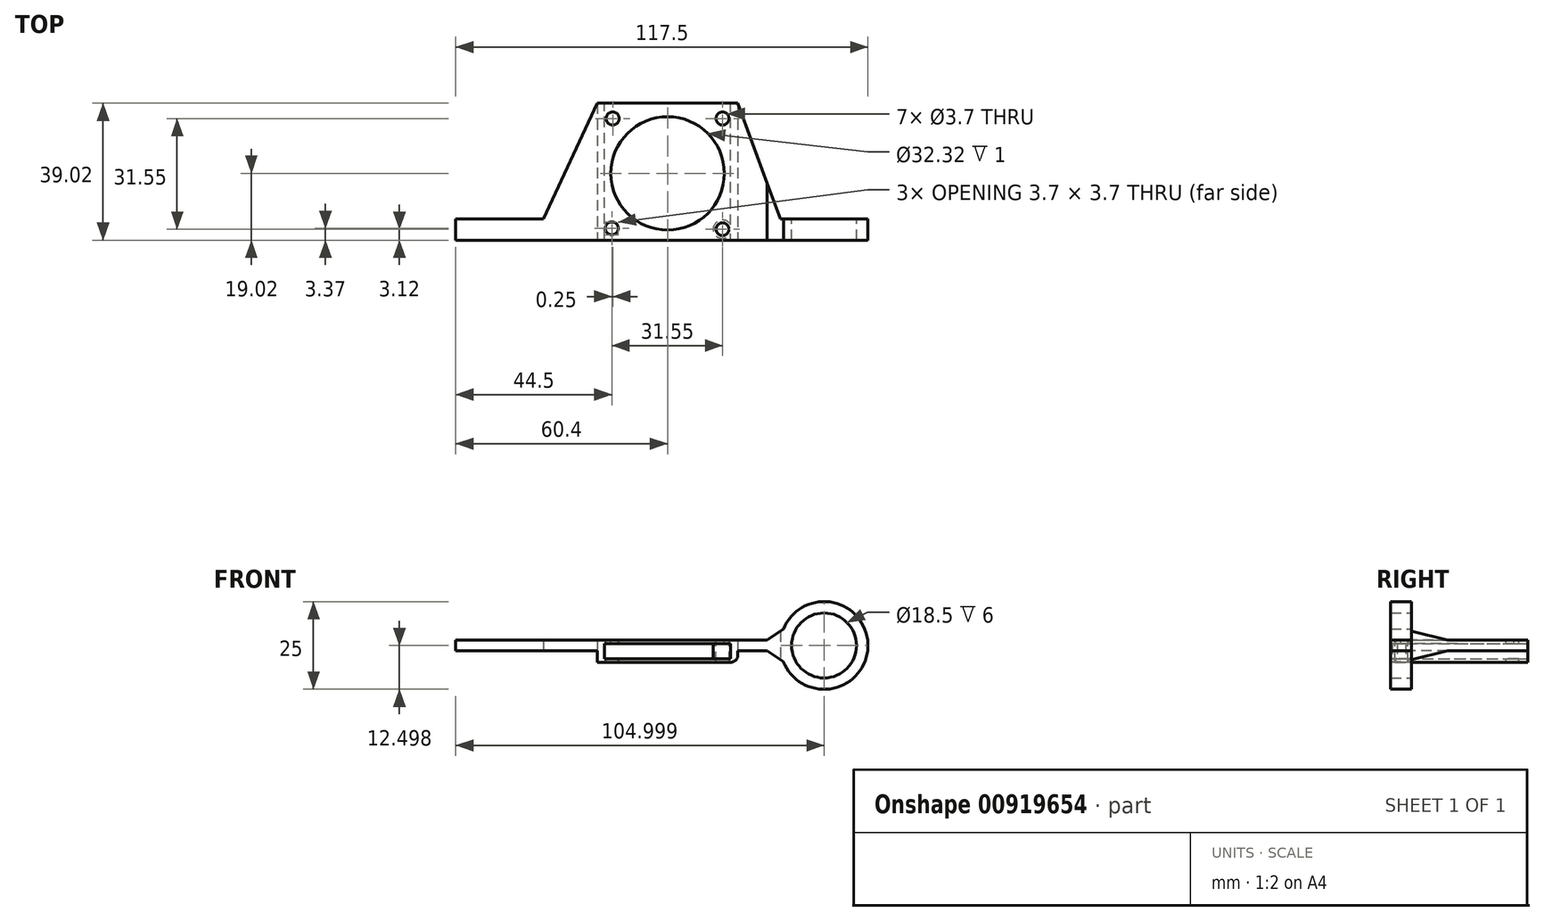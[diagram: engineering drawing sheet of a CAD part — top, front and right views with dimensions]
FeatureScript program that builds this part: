
annotation { "Feature Type Name" : "Feature", "Feature Type Description" : "" }
export const myFeature = defineFeature(function(context is Context, id is Id, definition is map)
    precondition{}
    {
        {
            var Q0;
            Q0=qCreatedBy(makeId("Top.planeOp"),FACE);
            var sketch = newSketch(context, id + "F0", { "sketchPlane" : qUnion([Q0])});
            skLineSegment(sketch, "E0", {"start": v(20, 20) * mm, "end": v(-20, 20) * mm});
            skLineSegment(sketch, "E1", {"start": v(48.76, 105.8) * mm, "end": v(3.76, 105.8) * mm});
            skLineSegment(sketch, "E2", {"start": v(20, 20) * mm, "end": v(32.1, -13.02) * mm});
            skLineSegment(sketch, "E3", {"start": v(57.1, -19.02) * mm, "end": v(57.1, -13.02) * mm});
            skLineSegment(sketch, "E4", {"start": v(57.1, -13.02) * mm, "end": v(32.1, -13.02) * mm});
            skLineSegment(sketch, "E5", {"start": v(-20, 20) * mm, "end": v(-35.4, -13.02) * mm});
            skLineSegment(sketch, "E6", {"start": v(-35.4, -13.02) * mm, "end": v(-60.4, -13.02) * mm});
            skLineSegment(sketch, "E7", {"start": v(-60.4, -13.02) * mm, "end": v(-60.4, -19.02) * mm});
            skLineSegment(sketch, "E8", {"start": v(-60.4, -19.02) * mm, "end": v(57.1, -19.02) * mm});
            skSolve(sketch);
        }
        {
            var Q0;
            Q0 = qSketchRegion(id + "F0", true);
            extrude(context, id + "F1", {"entities" : qUnion([Q0]), "depth" : 3 * mm, "offsetDistance" : 25 * mm});
        }
        {
            var Q0;
            Q0=makeQuery(id+"F1.opExtrude","SWEPT_FACE",FACE,{"disambiguationData":[OSD([sQuery(id+"F0.wireOp",EDGE,"E4")])]});
            var sketch = newSketch(context, id + "F2", { "sketchPlane" : qUnion([Q0])});
            skCircle(sketch, "E9", {"center": v(-44.6, 1.46) * mm, "radius": 12.5 * mm});
            skSolve(sketch);
        }
        {
            var Q0;
            Q0 = qSketchRegion(id + "F2", true);
            extrude(context, id + "F3", {"entities" : qUnion([Q0]), "operationType" : NewBodyOperationType.ADD, "oppositeDirection" : true, "depth" : 6 * mm, "offsetDistance" : 25 * mm});
        }
        {
            var Q0;
            Q0=makeQuery(id+"Fj0goD7DDU6lidK_1.boolean.opBoolean","MERGE",FACE,{"derivedFrom":[makeQuery(id+"F1.opExtrude","SWEPT_FACE",FACE,{"disambiguationData":[OSD([sQuery(id+"F0.wireOp",EDGE,"E4")])]}),makeQuery(id+"Fj0goD7DDU6lidK_1.opExtrude","CAP_FACE",FACE,{"disambiguationData":[OSD([sQuery(id+"F2.wireOp",EDGE,"E9")])],"isStart":true})]});
            var sketch = newSketch(context, id + "F4", { "sketchPlane" : qUnion([Q0])});
            skCircle(sketch, "E10", {"center": v(-44.6, 1.46) * mm, "radius": 9.25 * mm});
            skSolve(sketch);
        }
        {
            var Q0;
            Q0 = qSketchRegion(id + "F4", true);
            extrude(context, id + "F5", {"entities" : qUnion([Q0]), "operationType" : NewBodyOperationType.REMOVE, "oppositeDirection" : true, "depth" : 25 * mm, "offsetDistance" : 25 * mm});
        }
        {
            var Q0;
            {var subQ0=sQuery(id+"F0.wireOp",EDGE,"E8");var subQ1=sQuery(id+"F0.wireOp",EDGE,"E7");var subQ2=sQuery(id+"F0.wireOp",EDGE,"E6");var subQ3=sQuery(id+"F0.wireOp",EDGE,"E0");var subQ5=sQuery(id+"F0.wireOp",EDGE,"E4");var subQ6=sQuery(id+"F0.wireOp",EDGE,"E2");var subQ7=sQuery(id+"F0.wireOp",EDGE,"E5");Q0=makeQuery(id+"F3.boolean.opBoolean","SPLIT",FACE,{"disambiguationData":[TD([makeQuery(id+"F1.opExtrude","SWEPT_FACE",FACE,{"disambiguationData":[OSD([subQ3])]})])],"derivedFrom":makeQuery(id+"F1.opExtrude","CAP_FACE",FACE,{"disambiguationData":[OSD([subQ3,subQ6,sQuery(id+"F0.wireOp",EDGE,"E3"),subQ5,subQ7,subQ2,subQ1,subQ0])],"isStart":false})});}
            var sketch = newSketch(context, id + "F6", { "sketchPlane" : qUnion([Q0])});
            skCircle(sketch, "E11", {"center": v(0, 0) * mm, "radius": 16.16 * mm});
            skSolve(sketch);
        }
        {
            var Q0;
            Q0=makeQuery(id+"F6.imprint","IMPRINT",FACE,{"disambiguationData":[TD([[makeQuery(id+"F6.imprint","IMPRINT",EDGE,{"derivedFrom":sQuery(id+"F6.wireOp",EDGE,"E11")}),1.0]])]});
            extrude(context, id + "F7", {"entities" : qUnion([Q0]), "operationType" : NewBodyOperationType.REMOVE, "oppositeDirection" : true, "depth" : 25 * mm, "offsetDistance" : 25 * mm});
        }
        {
            var Q0;
            Q0=qCreatedBy(makeId("Right.planeOp"),FACE);
            var sketch = newSketch(context, id + "F8", { "sketchPlane" : qUnion([Q0])});
            skLineSegment(sketch, "E12.bottom", {"start": v(20, -3.33) * mm, "end": v(-19.02, -3.33) * mm});
            skLineSegment(sketch, "E12.top", {"start": v(20, 0) * mm, "end": v(-19.02, 0) * mm});
            skLineSegment(sketch, "E12.left", {"start": v(20, -3.33) * mm, "end": v(20, 0) * mm});
            skLineSegment(sketch, "E12.right", {"start": v(-19.02, -3.33) * mm, "end": v(-19.02, 0) * mm});
            skSolve(sketch);
        }
        {
            var Q0;
            Q0=makeQuery(id+"F8.imprint","IMPRINT",FACE,{"disambiguationData":[TD([[makeQuery(id+"F8.imprint","IMPRINT",EDGE,{"derivedFrom":sQuery(id+"F8.wireOp",EDGE,"E12.bottom")}),-1.0]])]});
            extrude(context, id + "F9", {"entities" : qUnion([Q0]), "operationType" : NewBodyOperationType.ADD, "depth" : 20 * mm, "offsetDistance" : 25 * mm, "hasSecondDirection" : true, "secondDirectionOppositeDirection" : true, "secondDirectionDepth" : 20 * mm});
        }
        {
            var Q0;
            Q0=makeQuery(id+"F9.boolean.opBoolean","MERGE",FACE,{"derivedFrom":[makeQuery(id+"F1.opExtrude","SWEPT_FACE",FACE,{"disambiguationData":[OSD([sQuery(id+"F0.wireOp",EDGE,"E0")])]}),makeQuery(id+"F9.opExtrude","SWEPT_FACE",FACE,{"disambiguationData":[OSD([sQuery(id+"F8.wireOp",EDGE,"E12.left")])]})]});
            var sketch = newSketch(context, id + "F10", { "sketchPlane" : qUnion([Q0])});
            skLineSegment(sketch, "E13.bottom", {"start": v(-18, 2) * mm, "end": v(18, 2) * mm});
            skLineSegment(sketch, "E13.top", {"start": v(-18, -2.33) * mm, "end": v(18, -2.33) * mm});
            skLineSegment(sketch, "E13.left", {"start": v(-18, 2) * mm, "end": v(-18, -2.33) * mm});
            skLineSegment(sketch, "E13.right", {"start": v(18, 2) * mm, "end": v(18, -2.33) * mm});
            skSolve(sketch);
        }
        {
            var Q0;
            Q0=makeQuery(id+"F10.imprint","IMPRINT",FACE,{"disambiguationData":[TD([[makeQuery(id+"F10.imprint","IMPRINT",EDGE,{"derivedFrom":sQuery(id+"F10.wireOp",EDGE,"E13.bottom")}),-1.0]])]});
            extrude(context, id + "F11", {"entities" : qUnion([Q0]), "operationType" : NewBodyOperationType.REMOVE, "endBound" : BoundingType.THROUGH_ALL, "oppositeDirection" : true, "depth" : 25 * mm, "offsetDistance" : 25 * mm});
        }
        {
            var Q0;
            Q0=makeQuery(id+"F1.opExtrude","CAP_FACE",FACE,{"disambiguationData":[OSD([sQuery(id+"F0.wireOp",EDGE,"KjVwb03s-ZiWv-Lm4M-7I9X-wJKAQ4s1qE5y"),sQuery(id+"F0.wireOp",EDGE,"oMOzuxQN-3AWz-xGX9-720S-HeuVsf5TF04R"),sQuery(id+"F0.wireOp",EDGE,"VBjpAbbY-30C4-MMW6-wtRy-WvcjqaOtYvMR"),sQuery(id+"F0.wireOp",EDGE,"HcxSt0mb-Gfiy-rUvU-8Zs3-hPTIjIVvTNFS"),sQuery(id+"F0.wireOp",EDGE,"wiUAUu8o-BY7j-2pSR-UUTj-5Hzk0u3y44G6"),sQuery(id+"F0.wireOp",EDGE,"E0")])],"isStart":false});
            var sketch = newSketch(context, id + "F12", { "sketchPlane" : qUnion([Q0])});
            skCircle(sketch, "E14", {"center": v(-15.65, 15.65) * mm, "radius": 1.85 * mm});
            skCircle(sketch, "E15", {"center": v(-15.9, -15.65) * mm, "radius": 1.85 * mm});
            skLineSegment(sketch, "E16", {"start": v(20, -20) * mm, "end": v(20, 20) * mm});
            skCircle(sketch, "E17", {"center": v(15.65, 15.65) * mm, "radius": 1.85 * mm});
            skCircle(sketch, "E18", {"center": v(15.65, -15.9) * mm, "radius": 1.85 * mm});
            skLineSegment(sketch, "E19", {"start": v(20, 20) * mm, "end": v(20, -20) * mm});
            skLineSegment(sketch, "E20", {"start": v(-20, 20) * mm, "end": v(-20, -19.02) * mm});
            skSolve(sketch);
        }
        {
            var Q0;
            Q0 = qSketchRegion(id + "F12", true);
            extrude(context, id + "F13", {"entities" : qUnion([Q0]), "operationType" : NewBodyOperationType.REMOVE, "endBound" : BoundingType.THROUGH_ALL, "oppositeDirection" : true, "depth" : 25 * mm, "offsetDistance" : 25 * mm});
        }
        {
            var Q0;
            Q0=makeQuery(id+"F9.opExtrude","CAP_EDGE",EDGE,{"disambiguationData":[OSD([sQuery(id+"F8.wireOp",EDGE,"E12.bottom")])],"isStart":false});
            fillet(context, id + "F14", {"entities" : qUnion([Q0]), "radius" : 2 * mm, "tangentPropagation" : true, "allowEdgeOverflow" : false});
        }
        {
            var Q0;
            Q0=makeQuery(id+"F9.opExtrude","SWEPT_FACE",FACE,{"disambiguationData":[OSD([sQuery(id+"F8.wireOp",EDGE,"E12.bottom")])]});
            var sketch = newSketch(context, id + "F15", { "sketchPlane" : qUnion([Q0])});
            skCircle(sketch, "E21", {"center": v(15.65, 15.9) * mm, "radius": 2.65 * mm});
            skSolve(sketch);
        }
        {
            var Q0;
            {var subQ1=sQuery(id+"F8.wireOp",EDGE,"E12.bottom");var subQ2=makeQuery(id+"F9.opExtrude","SWEPT_FACE",FACE,{"disambiguationData":[OSD([subQ1])]});Q0=makeQuery(id+"F15.imprint","IMPRINT",FACE,{"disambiguationData":[TD([[makeQuery(id+"F15.imprint","IMPRINT",EDGE,{"derivedFrom":makeQuery(id+"F13.boolean.opBoolean","INTERSECT",EDGE,{"derivedFrom":[subQ2,makeQuery(id+"F13.opExtrude","SWEPT_FACE",FACE,{"disambiguationData":[OSD([sQuery(id+"F12.wireOp",EDGE,"E18")])]})]})}),-1.0]])]});}
            var Q1;
            Q1=makeQuery(id+"F11.boolean.opBoolean","COPY",FACE,{"derivedFrom":makeQuery(id+"F11.opExtrude","SWEPT_FACE",FACE,{"disambiguationData":[OSD([sQuery(id+"F10.wireOp",EDGE,"E13.bottom")])]})});
            extrude(context, id + "F16", {"entities" : qUnion([Q0]), "operationType" : NewBodyOperationType.ADD, "endBound" : BoundingType.UP_TO_SURFACE, "oppositeDirection" : true, "depth" : 25 * mm, "endBoundEntityFace" : qUnion([Q1]), "offsetDistance" : 25 * mm});
        }
        {
            var Q0;
            {var subQ0=sQuery(id+"F2.wireOp",EDGE,"E9");var subQ1=sQuery(id+"F0.wireOp",EDGE,"E4");var subQ2=sQuery(id+"F0.wireOp",EDGE,"E2");var subQ3=makeQuery(id+"F1.opExtrude","SWEPT_EDGE",EDGE,{"disambiguationData":[OSD([subQ2,subQ1])]});var subQ4=makeQuery(id+"F1.opExtrude","CAP_EDGE",EDGE,{"disambiguationData":[OSD([subQ1])],"isStart":true});var subQ5=makeQuery(id+"F2.imprint","INTERSECT",VERTEX,{"disambiguationData":[OD(1.0)],"derivedFrom":[subQ4,subQ0]});var subQ6=makeQuery(id+"F2.imprint","INTERSECT",VERTEX,{"disambiguationData":[OD(0.0)],"derivedFrom":[subQ4,subQ0]});var subQ7=makeQuery(id+"F1.opExtrude","CAP_EDGE",EDGE,{"disambiguationData":[OSD([subQ1])],"isStart":false});var subQ8=makeQuery(id+"F2.imprint","INTERSECT",VERTEX,{"disambiguationData":[OD(1.0)],"derivedFrom":[subQ7,subQ0]});var subQ9=makeQuery(id+"F2.imprint","INTERSECT",VERTEX,{"disambiguationData":[OD(0.0)],"derivedFrom":[subQ7,subQ0]});Q0=makeQuery(id+"F3.boolean.opBoolean","INTERSECT",EDGE,{"disambiguationData":[OD(0.0)],"derivedFrom":[makeQuery(id+"F1.opExtrude","CAP_FACE",FACE,{"disambiguationData":[OSD([sQuery(id+"F0.wireOp",EDGE,"E0"),subQ2,sQuery(id+"F0.wireOp",EDGE,"E3"),subQ1,sQuery(id+"F0.wireOp",EDGE,"E5"),sQuery(id+"F0.wireOp",EDGE,"E6"),sQuery(id+"F0.wireOp",EDGE,"E7"),sQuery(id+"F0.wireOp",EDGE,"E8")])],"isStart":true}),makeQuery(id+"F3.opExtrude","SWEPT_FACE",FACE,{"disambiguationData":[OSD([subQ0]),TDD([makeQuery(id+"F2.imprint","IMPRINT",EDGE,{"disambiguationData":[TD([[makeQuery(id+"F2.imprint","INTERSECT",VERTEX,{"disambiguationData":[OD(0.0)],"derivedFrom":[subQ3,subQ0]}),-1.0],[subQ9,1.0]])],"derivedFrom":subQ0}),makeQuery(id+"F2.imprint","IMPRINT",EDGE,{"disambiguationData":[TD([[subQ9,-1.0],[subQ8,1.0]])],"derivedFrom":subQ0}),makeQuery(id+"F2.imprint","IMPRINT",EDGE,{"disambiguationData":[TD([[subQ8,-1.0],[subQ6,1.0]])],"derivedFrom":subQ0}),makeQuery(id+"F2.imprint","IMPRINT",EDGE,{"disambiguationData":[TD([[subQ6,-1.0],[subQ5,1.0]])],"derivedFrom":subQ0}),makeQuery(id+"F2.imprint","IMPRINT",EDGE,{"disambiguationData":[TD([[makeQuery(id+"F2.imprint","INTERSECT",VERTEX,{"disambiguationData":[OD(1.0)],"derivedFrom":[subQ3,subQ0]}),1.0],[subQ5,-1.0]])],"derivedFrom":subQ0})])]})]});}
            var Q1;
            {var subQ0=sQuery(id+"F2.wireOp",EDGE,"E9");var subQ1=sQuery(id+"F0.wireOp",EDGE,"E4");var subQ2=sQuery(id+"F0.wireOp",EDGE,"E2");var subQ3=makeQuery(id+"F1.opExtrude","SWEPT_EDGE",EDGE,{"disambiguationData":[OSD([subQ2,subQ1])]});var subQ4=makeQuery(id+"F1.opExtrude","CAP_EDGE",EDGE,{"disambiguationData":[OSD([subQ1])],"isStart":true});var subQ5=makeQuery(id+"F2.imprint","INTERSECT",VERTEX,{"disambiguationData":[OD(1.0)],"derivedFrom":[subQ4,subQ0]});var subQ6=makeQuery(id+"F2.imprint","INTERSECT",VERTEX,{"disambiguationData":[OD(0.0)],"derivedFrom":[subQ4,subQ0]});var subQ7=makeQuery(id+"F1.opExtrude","CAP_EDGE",EDGE,{"disambiguationData":[OSD([subQ1])],"isStart":false});var subQ8=makeQuery(id+"F2.imprint","INTERSECT",VERTEX,{"disambiguationData":[OD(1.0)],"derivedFrom":[subQ7,subQ0]});var subQ9=makeQuery(id+"F2.imprint","INTERSECT",VERTEX,{"disambiguationData":[OD(0.0)],"derivedFrom":[subQ7,subQ0]});Q1=makeQuery(id+"F3.boolean.opBoolean","INTERSECT",EDGE,{"disambiguationData":[OD(0.0)],"derivedFrom":[makeQuery(id+"F1.opExtrude","CAP_FACE",FACE,{"disambiguationData":[OSD([sQuery(id+"F0.wireOp",EDGE,"E0"),subQ2,sQuery(id+"F0.wireOp",EDGE,"E3"),subQ1,sQuery(id+"F0.wireOp",EDGE,"E5"),sQuery(id+"F0.wireOp",EDGE,"E6"),sQuery(id+"F0.wireOp",EDGE,"E7"),sQuery(id+"F0.wireOp",EDGE,"E8")])],"isStart":false}),makeQuery(id+"F3.opExtrude","SWEPT_FACE",FACE,{"disambiguationData":[OSD([subQ0]),TDD([makeQuery(id+"F2.imprint","IMPRINT",EDGE,{"disambiguationData":[TD([[makeQuery(id+"F2.imprint","INTERSECT",VERTEX,{"disambiguationData":[OD(0.0)],"derivedFrom":[subQ3,subQ0]}),-1.0],[subQ9,1.0]])],"derivedFrom":subQ0}),makeQuery(id+"F2.imprint","IMPRINT",EDGE,{"disambiguationData":[TD([[subQ9,-1.0],[subQ8,1.0]])],"derivedFrom":subQ0}),makeQuery(id+"F2.imprint","IMPRINT",EDGE,{"disambiguationData":[TD([[subQ8,-1.0],[subQ6,1.0]])],"derivedFrom":subQ0}),makeQuery(id+"F2.imprint","IMPRINT",EDGE,{"disambiguationData":[TD([[subQ6,-1.0],[subQ5,1.0]])],"derivedFrom":subQ0}),makeQuery(id+"F2.imprint","IMPRINT",EDGE,{"disambiguationData":[TD([[makeQuery(id+"F2.imprint","INTERSECT",VERTEX,{"disambiguationData":[OD(1.0)],"derivedFrom":[subQ3,subQ0]}),1.0],[subQ5,-1.0]])],"derivedFrom":subQ0})])]})]});}
            chamfer(context, id + "F17", {"entities" : qUnion([Q0, Q1]), "width" : 5 * mm, "tangentPropagation" : true});
        }
    });
